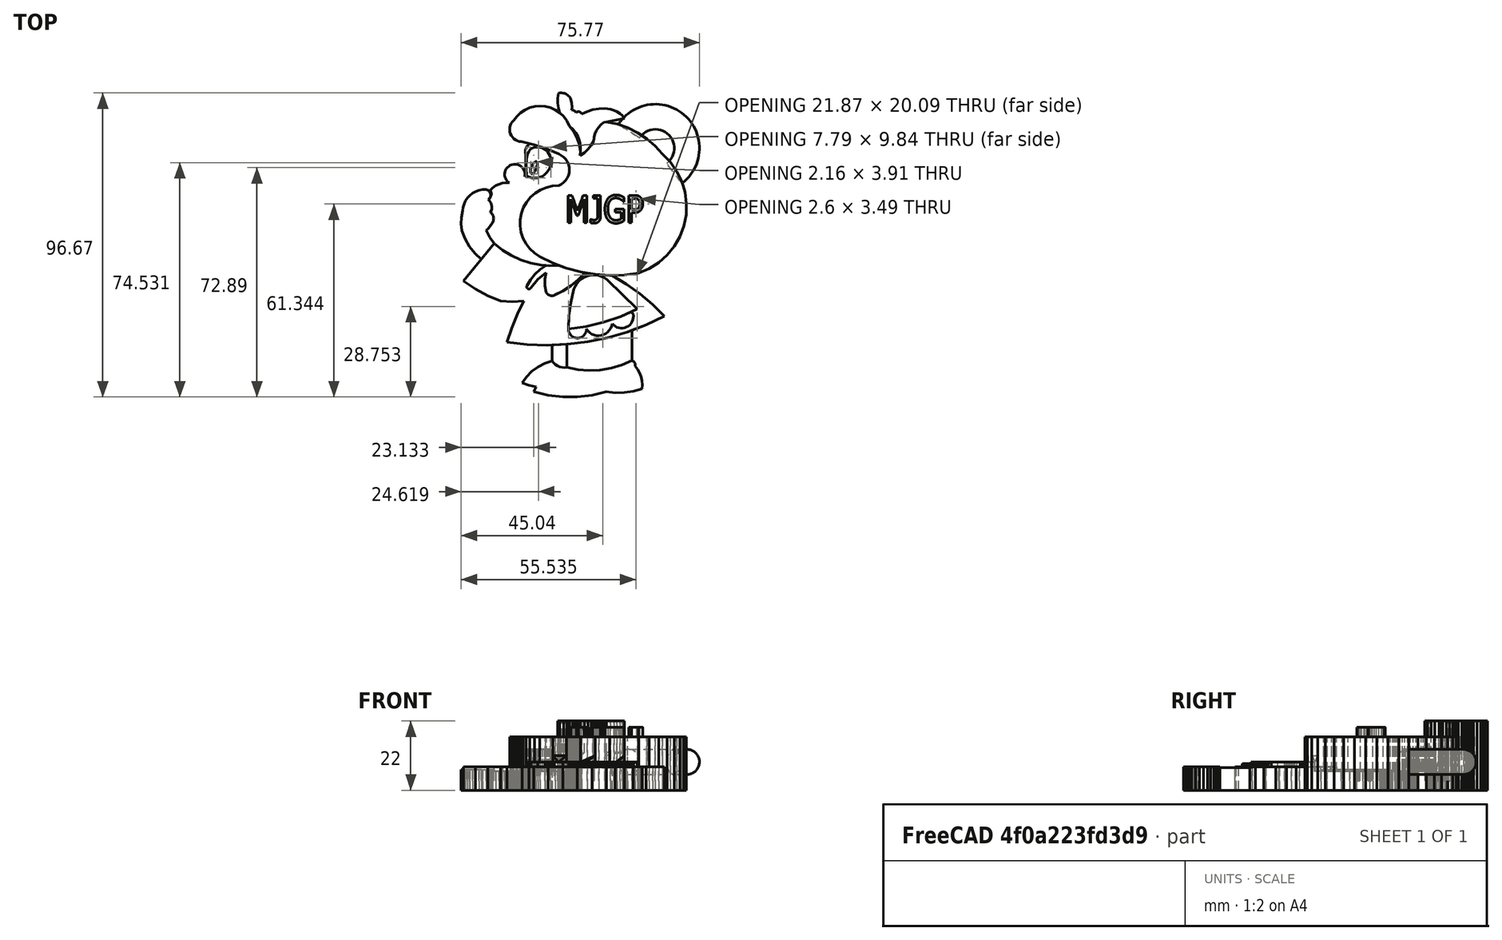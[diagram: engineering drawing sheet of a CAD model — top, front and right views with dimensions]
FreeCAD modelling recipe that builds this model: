
FCSTD DOCUMENT  (FreeCAD 0.18R4 (GitTag))
Label: mfd3freecad
License: All rights reserved
LicenseURL: http://en.wikipedia.org/wiki/All_rights_reserved
objects: Part::Feature×8, Part::Extrusion×5, PartDesign::Pad×3, Part::Compound×3, Sketcher::SketchObject×2, Mesh::Feature×1, PartDesign::Pocket×1, PartDesign::Body×1, Part::Torus×1, Part::Cut×1
note: 29 computed .brp shape members not serialized (recipe doc carries the construction recipe); baked Part::Feature solids carry a one-line shape summary decoded from their .brp

FEATURE [Mesh::Feature] mafalda_prueba_1
FEATURE [Part::Feature] mafalda_prueba_1001
  shape: bbox 92.2 x 12 x 121.8 mm, 2550 faces, 0 solids (baked)
FEATURE [Sketcher::SketchObject] Sketch
  MapMode = 5
  Placement = pos=(0,0,0) rot=(1,0,0;1.5708rad)
  Support = -> [XZ_Plane]
FEATURE [PartDesign::Pad] Pad
  Length = 6
  Length2 = 100
  Type = 0
FEATURE [PartDesign::Pad] Pad001
  BaseFeature = -> Pad
  Length = 10
  Length2 = 100
  Profile = -> Pad [Face351]
  Type = 0
FEATURE [Sketcher::SketchObject] Sketch001
  MapMode = 5
  Placement = pos=(0,3,0) rot=(0,0.707107,0.707107;3.14159rad)
  Support = -> [Pad001]
FEATURE [PartDesign::Pocket] Pocket
  BaseFeature = -> Pad001
  Length = 20
  Length2 = 100
  Profile = -> Pad001 [Face52]
  Type = 0
FEATURE [PartDesign::Pad] Pad002
  BaseFeature = -> Pocket
  Length = 6
  Length2 = 100
  Profile = -> Pocket [Face930]
  Type = 0
FEATURE [PartDesign::Body] Body
  Group = -> [Sketch,Pad,Pad001,Sketch001,Pocket,Pad002]
  Origin = -> Origin
  Placement = pos=(0,115,0) rot=(1,0,0;1.5708rad)
  Tip = -> Pad002
FEATURE [Part::Torus] Torus  label="Toro"
  Angle1 = -180
  Angle2 = 180
  Angle3 = 200
  AttacherType = Attacher::AttachEngine3D
  Placement = pos=(74,87,9) rot=(0,0,-1;0.925025rad)
  Radius1 = 10
  Radius2 = 4
FEATURE [Part::Compound] Compound
  Links = -> [Body,Torus]
FEATURE [Part::Feature] Compound001
  shape: bbox 76.78 x 96.66 x 22 mm, 632 faces, 2 solids (baked)
FEATURE [Part::Feature] path1518
  shape: bbox 6.041 x 8.728 x 4.006e-07 mm, 0 faces, 0 solids (baked)
FEATURE [Part::Feature] path1520
  shape: bbox 3.198 x 8.851 x 4.006e-07 mm, 0 faces, 0 solids (baked)
FEATURE [Part::Feature] path1522
  shape: bbox 6.046 x 9.056 x 4.006e-07 mm, 0 faces, 0 solids (baked)
FEATURE [Part::Feature] path1524
  shape: bbox 4.437 x 8.728 x 4.006e-07 mm, 0 faces, 0 solids (baked)
FEATURE [Part::Feature] path1524001
  shape: bbox 2.597 x 3.488 x 4.006e-07 mm, 0 faces, 0 solids (baked)
FEATURE [Part::Extrusion] Extrude
  Base = -> path1518
  Dir = (0,0,-1)
  DirMode = 2
  FaceMakerClass = Part::FaceMakerBullseye
  LengthFwd = 3
  LengthRev = 0
  Solid = true
  Symmetric = false
FEATURE [Part::Extrusion] Extrude001
  Base = -> path1520
  Dir = (0,0,-1)
  DirMode = 2
  FaceMakerClass = Part::FaceMakerBullseye
  LengthFwd = 3
  LengthRev = 0
  Solid = true
  Symmetric = false
FEATURE [Part::Extrusion] Extrude002
  Base = -> path1522
  Dir = (0,0,-1)
  DirMode = 2
  FaceMakerClass = Part::FaceMakerBullseye
  LengthFwd = 3
  LengthRev = 0
  Solid = true
  Symmetric = false
FEATURE [Part::Extrusion] Extrude003
  Base = -> path1524
  Dir = (0,0,-1)
  DirMode = 2
  FaceMakerClass = Part::FaceMakerBullseye
  LengthFwd = 3
  LengthRev = 0
  Solid = true
  Symmetric = false
FEATURE [Part::Extrusion] Extrude004
  Base = -> path1524001
  Dir = (0,0,1)
  DirMode = 2
  FaceMakerClass = Part::FaceMakerBullseye
  LengthFwd = 10
  LengthRev = 0
  Placement = pos=(0,0,-7) rot=(0,0,1;0rad)
  Solid = true
  Symmetric = false
FEATURE [Part::Cut] Cut
  Base = -> Extrude003
  Refine = true
  Tool = -> Extrude004
FEATURE [Part::Compound] Compound002
  Links = -> [Extrude,Extrude001,Extrude002,Cut]
  Placement = pos=(43,75,20) rot=(0,0,1;0rad)
FEATURE [Part::Compound] Compound003
  Links = -> [Compound001,Compound002]
FEATURE [Part::Feature] Compound003001  label="Compound004"
  shape: bbox 76.78 x 96.66 x 22 mm, 723 faces, 6 solids (baked)
